# Revit family: QF_TRUE_TDM-R-59_cat
name_source: partatom
category: Specialty Equipment
revit_build: Autodesk Revit 2014 (Build: 20130308_1515(x64)
units: mm (PartAtom-declared; Revit-internal decimal feet)

## types (1)
- QF_TRUE_TDM-R-59_cat
    Apparent Power = 0 VA
    Conn Conduit = Yes
    Conn Plug = 5-15P
    Cycle = 60 Hz
    Depth = 39"
    Description = CURVED GLASS, GLASS END REFRIGERATOR
    Elec Conn Connection Height = 0"
    Elec Conn RI Height = 0"
    Exterior Finishes = QF_Plastic - Black - Coarse Textured
    FL Amps = 12 A
    Foodservice Equipment Identifier = Yes
    Glass End = Yes
    HP = 1/2
    Height = 49 1/8"
    Identify Quantity as Lot = Yes
    Interior Finishes = QF_Plastic - White - Smooth
    Length = 59 1/4"
    Manufacturer = TRUE
    Max Overcurrent Protection = 0 A
    Min Ckt Ampacity = 0 A
    Mirror End = No
    Model = TDM-R-59
    Number of Poles = 1
    Pass Code = 1
    Phase = 1
    Solid Mirror End = No
    Volts = 115 V
    Watts = 1380 W
    Weight in Pounds = 760

## geometry (parser evidence)
native form markers: Blend x10, Sweep x2
no freeform markers — native parametric forms only
